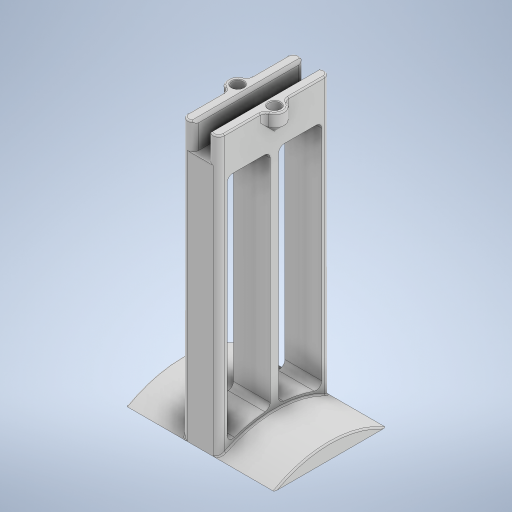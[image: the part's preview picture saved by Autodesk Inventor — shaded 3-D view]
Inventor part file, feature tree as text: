
AUTODESK INVENTOR PART (.ipt)
format: ipt  version: 2024.2 (Build 282272000, 272)  size: 451,584 bytes
history: native  units: mm
features: extrude x6, fillet x4, chamfer x3, plane x1, mirror x1
ambient origin geometry x8: Origin, YZ Plane, XZ Plane, XY Plane, X Axis, Y Axis, Z Axis, Center Point
bodies: Solid1 (feature_tree)
feature tree (15):
  extrude  "Extrusion1"  Depth=100.0mm
  extrude  "Extrusion2"  Depth=40.0mm
  plane  "Work Plane1"
  mirror  "Mirror1"
  extrude  "Extrusion3"  Depth=13.2mm TaperAngle=0.0deg
  extrude  "Extrusion4"  Depth=20.0mm TaperAngle=0.0deg
  extrude  "Extrusion5"  [1 undecoded]
  extrude  "Extrusion6"  Depth=5.2mm
  chamfer  "Chamfer2"  Distance=4.0mm
  fillet  "Fillet1"  Radius=9.6mm
  chamfer  "Chamfer1"  Distance=2.0mm
  fillet  "Fillet2"  Radius=2.0mm
  fillet  "Fillet3"  Radius=4.1mm
  chamfer  "Chamfer3"  Distance=7.0mm
  fillet  "Fillet4"  Radius=8.0mm
note: 1 required parameter value undecoded (feature->parameter linkage not recoverable at this tier; creation-order binding heuristic only, values carry confidence <= 0.55)
